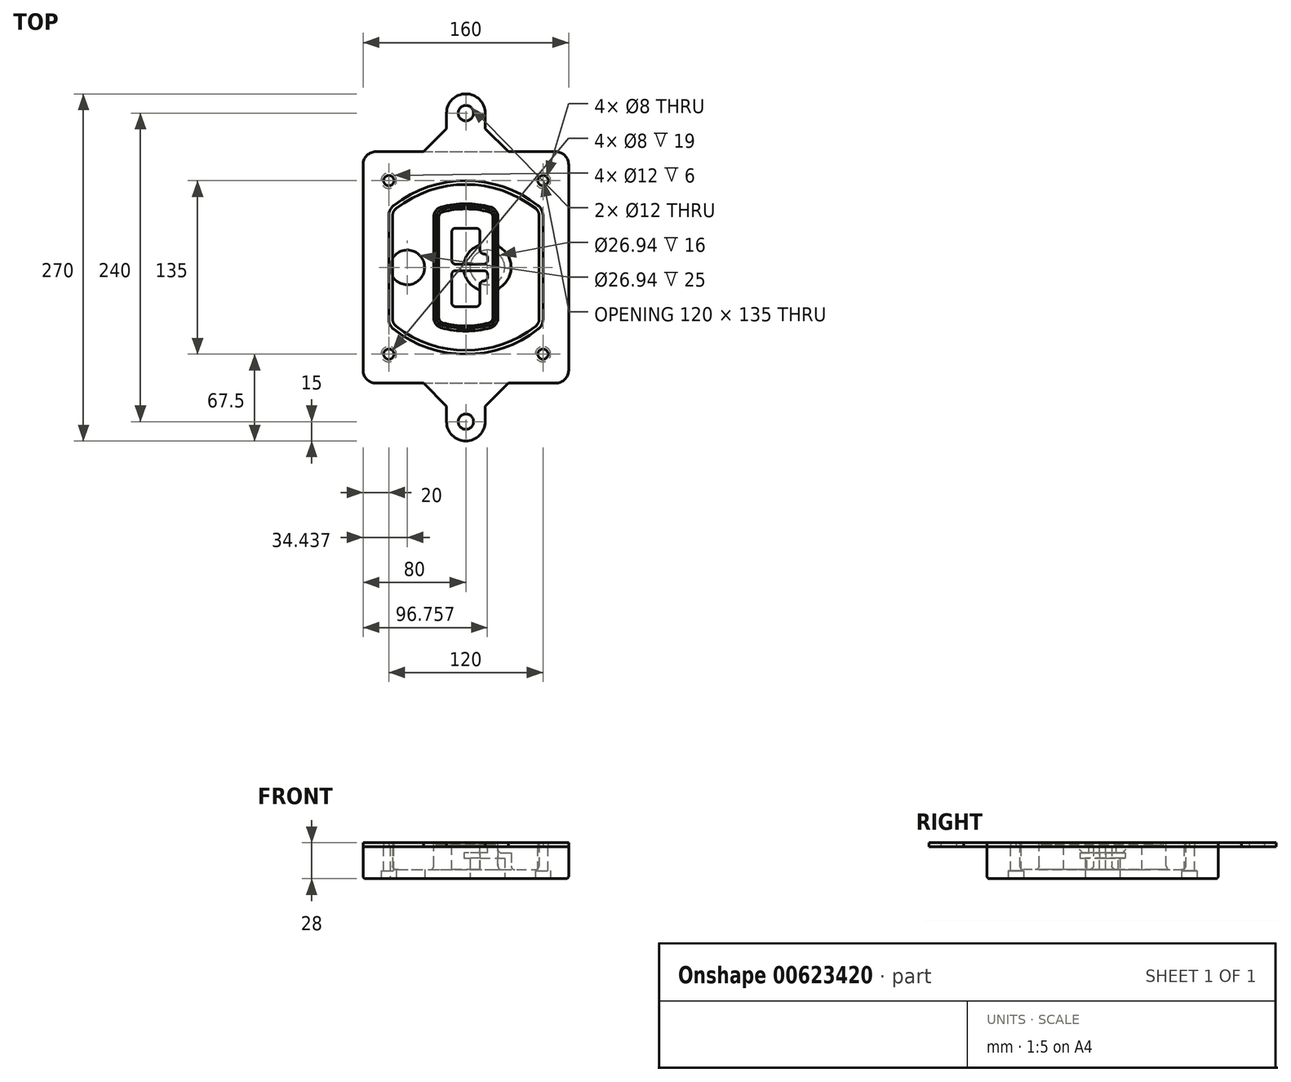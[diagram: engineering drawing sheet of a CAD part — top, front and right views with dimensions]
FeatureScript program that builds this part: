
annotation { "Feature Type Name" : "Feature", "Feature Type Description" : "" }
export const myFeature = defineFeature(function(context is Context, id is Id, definition is map)
    precondition{}
    {
        {
            var Q0;
            Q0=qCreatedBy(makeId("Top.planeOp"),FACE);
            var sketch = newSketch(context, id + "F0", { "sketchPlane" : qUnion([Q0])});
            skPoint(sketch, "E0.rect.middle", {"position": v(0, 0) * mm});
            skLineSegment(sketch, "E1.bottom", {"start": v(-70, -90) * mm, "end": v(70, -90) * mm});
            skLineSegment(sketch, "E1.top", {"start": v(-70, 90) * mm, "end": v(70, 90) * mm});
            skLineSegment(sketch, "E1.left", {"start": v(-80, -80) * mm, "end": v(-80, 80) * mm});
            skLineSegment(sketch, "E1.right", {"start": v(80, -80) * mm, "end": v(80, 80) * mm});
            skLineSegment(sketch, "E2", {"start": v(-80, 90) * mm, "end": v(80, -90) * mm, "construction": true});
            skLineSegment(sketch, "E3", {"start": v(80, 90) * mm, "end": v(-80, -90) * mm, "construction": true});
            skCircle(sketch, "E4", {"center": v(-60, 67.5) * mm, "radius": 4 * mm});
            skCircle(sketch, "E5", {"center": v(60, 67.5) * mm, "radius": 4 * mm});
            skCircle(sketch, "E6", {"center": v(60, -67.5) * mm, "radius": 4 * mm});
            skCircle(sketch, "E7", {"center": v(-60, -67.5) * mm, "radius": 4 * mm});
            skLineSegment(sketch, "E8", {"start": v(-60, 67.5) * mm, "end": v(60, 67.5) * mm, "construction": true});
            skLineSegment(sketch, "E9", {"start": v(60, 67.5) * mm, "end": v(60, -67.5) * mm, "construction": true});
            skLineSegment(sketch, "E10", {"start": v(60, -67.5) * mm, "end": v(-60, -67.5) * mm, "construction": true});
            skLineSegment(sketch, "E11", {"start": v(-60, -67.5) * mm, "end": v(-60, 67.5) * mm, "construction": true});
            skLineSegment(sketch, "E12", {"start": v(-60, 40.3) * mm, "end": v(-60, -40.3) * mm});
            skLineSegment(sketch, "E13", {"start": v(60, 40.3) * mm, "end": v(60, -40.3) * mm});
            skArc(sketch, "E14", {"start": v(56.15, 48.18) * mm, "mid": v(0, 67.5) * mm, "end": v(-56.15, 48.18) * mm});
            skArc(sketch, "E15", {"start": v(-56.15, -48.18) * mm, "mid": v(0, -67.5) * mm, "end": v(56.15, -48.18) * mm});
            skLineSegment(sketch, "E16", {"start": v(-60, 0) * mm, "end": v(60, 0) * mm, "construction": true});
            skPoint(sketch, "E17.visualSharp", {"position": v(-60, -45) * mm});
            skArc(sketch, "E17.filletArc", {"start": v(-60, -40.3) * mm, "mid": v(-58.99, -44.68) * mm, "end": v(-56.15, -48.18) * mm});
            skPoint(sketch, "E18.visualSharp", {"position": v(-60, 45) * mm});
            skArc(sketch, "E18.filletArc", {"start": v(-56.15, 48.18) * mm, "mid": v(-58.99, 44.68) * mm, "end": v(-60, 40.3) * mm});
            skPoint(sketch, "E19.visualSharp", {"position": v(60, 45) * mm});
            skArc(sketch, "E19.filletArc", {"start": v(60, 40.3) * mm, "mid": v(58.99, 44.68) * mm, "end": v(56.15, 48.18) * mm});
            skPoint(sketch, "E20.visualSharp", {"position": v(60, -45) * mm});
            skArc(sketch, "E20.filletArc", {"start": v(56.15, -48.18) * mm, "mid": v(58.99, -44.68) * mm, "end": v(60, -40.3) * mm});
            skPoint(sketch, "E21.visualSharp", {"position": v(-80, 90) * mm});
            skArc(sketch, "E21.filletArc", {"start": v(-70, 90) * mm, "mid": v(-77.07, 87.07) * mm, "end": v(-80, 80) * mm});
            skPoint(sketch, "E22.visualSharp", {"position": v(80, 90) * mm});
            skArc(sketch, "E22.filletArc", {"start": v(80, 80) * mm, "mid": v(77.07, 87.07) * mm, "end": v(70, 90) * mm});
            skPoint(sketch, "E23.visualSharp", {"position": v(80, -90) * mm});
            skArc(sketch, "E23.filletArc", {"start": v(70, -90) * mm, "mid": v(77.07, -87.07) * mm, "end": v(80, -80) * mm});
            skPoint(sketch, "E24.visualSharp", {"position": v(-80, -90) * mm});
            skArc(sketch, "E24.filletArc", {"start": v(-80, -80) * mm, "mid": v(-77.07, -87.07) * mm, "end": v(-70, -90) * mm});
            skArc(sketch, "E25.0", {"start": v(57, 40.3) * mm, "mid": v(56.3, 43.36) * mm, "end": v(54.3, 45.81) * mm});
            skLineSegment(sketch, "E25.1", {"start": v(57, 40.3) * mm, "end": v(57, -40.3) * mm});
            skArc(sketch, "E25.2", {"start": v(54.3, -45.81) * mm, "mid": v(56.3, -43.36) * mm, "end": v(57, -40.3) * mm});
            skArc(sketch, "E25.3", {"start": v(-54.3, -45.81) * mm, "mid": v(0, -64.5) * mm, "end": v(54.3, -45.81) * mm});
            skArc(sketch, "E25.4", {"start": v(-57, -40.3) * mm, "mid": v(-56.3, -43.36) * mm, "end": v(-54.3, -45.81) * mm});
            skArc(sketch, "E25.5", {"start": v(54.3, 45.81) * mm, "mid": v(0, 64.5) * mm, "end": v(-54.3, 45.81) * mm});
            skLineSegment(sketch, "E25.6", {"start": v(-57, 40.3) * mm, "end": v(-57, -40.3) * mm});
            skArc(sketch, "E25.7", {"start": v(-54.3, 45.81) * mm, "mid": v(-56.3, 43.36) * mm, "end": v(-57, 40.3) * mm});
            skArc(sketch, "E26.0", {"start": v(-58.62, 51.33) * mm, "mid": v(-62.58, 46.43) * mm, "end": v(-64, 40.3) * mm});
            skArc(sketch, "E26.1", {"start": v(58.62, 51.33) * mm, "mid": v(0, 71.5) * mm, "end": v(-58.62, 51.33) * mm});
            skArc(sketch, "E26.2", {"start": v(64, 40.3) * mm, "mid": v(62.58, 46.43) * mm, "end": v(58.62, 51.33) * mm});
            skLineSegment(sketch, "E26.3", {"start": v(64, 40.3) * mm, "end": v(64, -40.3) * mm});
            skArc(sketch, "E26.4", {"start": v(58.62, -51.33) * mm, "mid": v(62.58, -46.43) * mm, "end": v(64, -40.3) * mm});
            skLineSegment(sketch, "E26.5", {"start": v(-64, 40.3) * mm, "end": v(-64, -40.3) * mm});
            skArc(sketch, "E26.6", {"start": v(-58.62, -51.33) * mm, "mid": v(0, -71.5) * mm, "end": v(58.62, -51.33) * mm});
            skArc(sketch, "E26.7", {"start": v(-64, -40.3) * mm, "mid": v(-62.58, -46.43) * mm, "end": v(-58.62, -51.33) * mm});
            skSolve(sketch);
        }
        {
            var Q0;
            Q0=makeQuery(id+"F0.imprint","IMPRINT",FACE,{"disambiguationData":[TD([[makeQuery(id+"F0.imprint","IMPRINT",EDGE,{"derivedFrom":sQuery(id+"F0.wireOp",EDGE,"E1.bottom")}),1.0]])]});
            var Q1;
            Q1=makeQuery(id+"F0.imprint","IMPRINT",FACE,{"disambiguationData":[TD([[makeQuery(id+"F0.imprint","IMPRINT",EDGE,{"derivedFrom":sQuery(id+"F0.wireOp",EDGE,"E12")}),1.0]])]});
            var Q2;
            Q2=makeQuery(id+"F0.imprint","IMPRINT",FACE,{"disambiguationData":[TD([[makeQuery(id+"F0.imprint","IMPRINT",EDGE,{"derivedFrom":sQuery(id+"F0.wireOp",EDGE,"E25.0")}),1.0]])]});
            var Q3;
            Q3=makeQuery(id+"F0.imprint","IMPRINT",FACE,{"disambiguationData":[TD([[makeQuery(id+"F0.imprint","IMPRINT",EDGE,{"derivedFrom":sQuery(id+"F0.wireOp",EDGE,"E12")}),-1.0]])]});
            extrude(context, id + "F1", {"entities" : qUnion([Q0, Q1, Q2, Q3]), "oppositeDirection" : true, "depth" : 25 * mm});
        }
        {
            var Q0;
            Q0=makeQuery(id+"F0.imprint","IMPRINT",FACE,{"disambiguationData":[TD([[makeQuery(id+"F0.imprint","IMPRINT",EDGE,{"derivedFrom":sQuery(id+"F0.wireOp",EDGE,"E12")}),1.0]])]});
            extrude(context, id + "F2", {"entities" : qUnion([Q0]), "operationType" : NewBodyOperationType.ADD, "depth" : 3 * mm});
        }
        {
            var Q0;
            Q0=makeQuery(id+"F0.imprint","IMPRINT",FACE,{"disambiguationData":[TD([[makeQuery(id+"F0.imprint","IMPRINT",EDGE,{"derivedFrom":sQuery(id+"F0.wireOp",EDGE,"E25.0")}),1.0]])]});
            extrude(context, id + "F3", {"entities" : qUnion([Q0]), "operationType" : NewBodyOperationType.REMOVE, "oppositeDirection" : true, "depth" : 18 * mm});
        }
        {
            var Q0;
            Q0=makeQuery(id+"F2.opExtrude","CAP_FACE",FACE,{"disambiguationData":[OSD([sQuery(id+"F0.wireOp",EDGE,"E12"),sQuery(id+"F0.wireOp",EDGE,"E13"),sQuery(id+"F0.wireOp",EDGE,"E14"),sQuery(id+"F0.wireOp",EDGE,"E15"),sQuery(id+"F0.wireOp",EDGE,"E17.filletArc"),sQuery(id+"F0.wireOp",EDGE,"E18.filletArc"),sQuery(id+"F0.wireOp",EDGE,"E19.filletArc"),sQuery(id+"F0.wireOp",EDGE,"E20.filletArc"),sQuery(id+"F0.wireOp",EDGE,"E25.0"),sQuery(id+"F0.wireOp",EDGE,"E25.1"),sQuery(id+"F0.wireOp",EDGE,"E25.2"),sQuery(id+"F0.wireOp",EDGE,"E25.3"),sQuery(id+"F0.wireOp",EDGE,"E25.4"),sQuery(id+"F0.wireOp",EDGE,"E25.5"),sQuery(id+"F0.wireOp",EDGE,"E25.6"),sQuery(id+"F0.wireOp",EDGE,"E25.7")])],"isStart":false});
            var sketch = newSketch(context, id + "F4", { "sketchPlane" : qUnion([Q0])});
            skArc(sketch, "E27.0", {"start": v(-19.08, -46.97) * mm, "mid": v(0, -49.5) * mm, "end": v(19.08, -46.97) * mm});
            skArc(sketch, "E28.0", {"start": v(19.08, 46.97) * mm, "mid": v(0, 49.5) * mm, "end": v(-19.08, 46.97) * mm});
            skLineSegment(sketch, "E29", {"start": v(-25, 39.25) * mm, "end": v(-25, -39.25) * mm});
            skLineSegment(sketch, "E30", {"start": v(25, 39.25) * mm, "end": v(25, -39.25) * mm});
            skLineSegment(sketch, "E31", {"start": v(-25, 45.1) * mm, "end": v(25, 45.1) * mm, "construction": true});
            skLineSegment(sketch, "E32", {"start": v(-25, -45.1) * mm, "end": v(25, -45.1) * mm, "construction": true});
            skPoint(sketch, "E33.visualSharp", {"position": v(-25, 45.1) * mm});
            skArc(sketch, "E33.filletArc", {"start": v(-19.08, 46.97) * mm, "mid": v(-23.35, 44.11) * mm, "end": v(-25, 39.25) * mm});
            skPoint(sketch, "E34.visualSharp", {"position": v(25, 45.1) * mm});
            skArc(sketch, "E34.filletArc", {"start": v(25, 39.25) * mm, "mid": v(23.35, 44.11) * mm, "end": v(19.08, 46.97) * mm});
            skPoint(sketch, "E35.visualSharp", {"position": v(25, -45.1) * mm});
            skArc(sketch, "E35.filletArc", {"start": v(19.08, -46.97) * mm, "mid": v(23.35, -44.11) * mm, "end": v(25, -39.25) * mm});
            skPoint(sketch, "E36.visualSharp", {"position": v(-25, -45.1) * mm});
            skArc(sketch, "E36.filletArc", {"start": v(-25, -39.25) * mm, "mid": v(-23.35, -44.11) * mm, "end": v(-19.08, -46.97) * mm});
            skArc(sketch, "E37.0", {"start": v(54.3, 45.81) * mm, "mid": v(0, 64.5) * mm, "end": v(-54.3, 45.81) * mm});
            skArc(sketch, "E37.1", {"start": v(-54.3, 45.81) * mm, "mid": v(-56.3, 43.36) * mm, "end": v(-57, 40.3) * mm});
            skLineSegment(sketch, "E37.2", {"start": v(-57, 40.3) * mm, "end": v(-57, -40.3) * mm});
            skArc(sketch, "E37.3", {"start": v(-57, -40.3) * mm, "mid": v(-56.3, -43.36) * mm, "end": v(-54.3, -45.81) * mm});
            skArc(sketch, "E37.4", {"start": v(-54.3, -45.81) * mm, "mid": v(0, -64.5) * mm, "end": v(54.3, -45.81) * mm});
            skArc(sketch, "E37.5", {"start": v(54.3, -45.81) * mm, "mid": v(56.3, -43.36) * mm, "end": v(57, -40.3) * mm});
            skLineSegment(sketch, "E37.6", {"start": v(57, 40.3) * mm, "end": v(57, -40.3) * mm});
            skArc(sketch, "E37.7", {"start": v(57, 40.3) * mm, "mid": v(56.3, 43.36) * mm, "end": v(54.3, 45.81) * mm});
            skLineSegment(sketch, "E38.0", {"start": v(23, 39.25) * mm, "end": v(23, -39.25) * mm});
            skArc(sketch, "E38.1", {"start": v(18.56, -45.04) * mm, "mid": v(21.76, -42.9) * mm, "end": v(23, -39.25) * mm});
            skArc(sketch, "E38.2", {"start": v(-18.56, -45.04) * mm, "mid": v(0, -47.5) * mm, "end": v(18.56, -45.04) * mm});
            skArc(sketch, "E38.3", {"start": v(-23, -39.25) * mm, "mid": v(-21.76, -42.9) * mm, "end": v(-18.56, -45.04) * mm});
            skLineSegment(sketch, "E38.4", {"start": v(-23, 39.25) * mm, "end": v(-23, -39.25) * mm});
            skArc(sketch, "E38.5", {"start": v(23, 39.25) * mm, "mid": v(21.76, 42.9) * mm, "end": v(18.56, 45.04) * mm});
            skArc(sketch, "E38.6", {"start": v(-18.56, 45.04) * mm, "mid": v(-21.76, 42.9) * mm, "end": v(-23, 39.25) * mm});
            skArc(sketch, "E38.7", {"start": v(18.56, 45.04) * mm, "mid": v(0, 47.5) * mm, "end": v(-18.56, 45.04) * mm});
            skArc(sketch, "E39.0", {"start": v(21, 39.25) * mm, "mid": v(20.18, 41.68) * mm, "end": v(18.04, 43.1) * mm});
            skLineSegment(sketch, "E39.1", {"start": v(21, 39.25) * mm, "end": v(21, -39.25) * mm});
            skArc(sketch, "E39.2", {"start": v(18.04, -43.1) * mm, "mid": v(20.18, -41.68) * mm, "end": v(21, -39.25) * mm});
            skArc(sketch, "E39.3", {"start": v(-18.04, -43.1) * mm, "mid": v(0, -45.5) * mm, "end": v(18.04, -43.1) * mm});
            skArc(sketch, "E39.4", {"start": v(-21, -39.25) * mm, "mid": v(-20.18, -41.68) * mm, "end": v(-18.04, -43.1) * mm});
            skArc(sketch, "E39.5", {"start": v(18.04, 43.1) * mm, "mid": v(0, 45.5) * mm, "end": v(-18.04, 43.1) * mm});
            skLineSegment(sketch, "E39.6", {"start": v(-21, 39.25) * mm, "end": v(-21, -39.25) * mm});
            skArc(sketch, "E39.7", {"start": v(-18.04, 43.1) * mm, "mid": v(-20.18, 41.68) * mm, "end": v(-21, 39.25) * mm});
            skLineSegment(sketch, "E40", {"start": v(-25, 0) * mm, "end": v(25, 0) * mm, "construction": true});
            skLineSegment(sketch, "E41", {"start": v(-11, 5.5) * mm, "end": v(-11, 27.5) * mm});
            skLineSegment(sketch, "E42", {"start": v(-8, 30.5) * mm, "end": v(8, 30.5) * mm});
            skLineSegment(sketch, "E43", {"start": v(11, 27.5) * mm, "end": v(11, 13.5) * mm});
            skLineSegment(sketch, "E44", {"start": v(14, 10.5) * mm, "end": v(14, 10.5) * mm});
            skLineSegment(sketch, "E45", {"start": v(17, 7.5) * mm, "end": v(17, 5.5) * mm});
            skLineSegment(sketch, "E46", {"start": v(14, 2.5) * mm, "end": v(-8, 2.5) * mm});
            skPoint(sketch, "E47.visualSharp", {"position": v(-11, 30.5) * mm});
            skArc(sketch, "E47.filletArc", {"start": v(-8, 30.5) * mm, "mid": v(-10.12, 29.62) * mm, "end": v(-11, 27.5) * mm});
            skPoint(sketch, "E48.visualSharp", {"position": v(11, 30.5) * mm});
            skArc(sketch, "E48.filletArc", {"start": v(11, 27.5) * mm, "mid": v(10.12, 29.62) * mm, "end": v(8, 30.5) * mm});
            skPoint(sketch, "E49.visualSharp", {"position": v(11, 10.5) * mm});
            skArc(sketch, "E49.filletArc", {"start": v(11, 13.5) * mm, "mid": v(11.88, 11.38) * mm, "end": v(14, 10.5) * mm});
            skPoint(sketch, "E50.visualSharp", {"position": v(17, 10.5) * mm});
            skArc(sketch, "E50.filletArc", {"start": v(17, 7.5) * mm, "mid": v(16.12, 9.62) * mm, "end": v(14, 10.5) * mm});
            skPoint(sketch, "E51.visualSharp", {"position": v(17, 2.5) * mm});
            skArc(sketch, "E51.filletArc", {"start": v(14, 2.5) * mm, "mid": v(16.12, 3.38) * mm, "end": v(17, 5.5) * mm});
            skPoint(sketch, "E52.visualSharp", {"position": v(-11, 2.5) * mm});
            skArc(sketch, "E52.filletArc", {"start": v(-11, 5.5) * mm, "mid": v(-10.12, 3.38) * mm, "end": v(-8, 2.5) * mm});
            skLineSegment(sketch, "E53.0.MirrorCS", {"start": v(14, -2.5) * mm, "end": v(-8, -2.5) * mm});
            skArc(sketch, "E54.0.MirrorCS", {"start": v(-11, -5.5) * mm, "mid": v(-10.12, -3.38) * mm, "end": v(-8, -2.5) * mm});
            skLineSegment(sketch, "E55.0.MirrorCS", {"start": v(-11, -5.5) * mm, "end": v(-11, -27.5) * mm});
            skArc(sketch, "E56.0.MirrorCS", {"start": v(-8, -30.5) * mm, "mid": v(-10.12, -29.62) * mm, "end": v(-11, -27.5) * mm});
            skLineSegment(sketch, "E57.0.MirrorCS", {"start": v(-8, -30.5) * mm, "end": v(8, -30.5) * mm});
            skArc(sketch, "E58.0.MirrorCS", {"start": v(11, -27.5) * mm, "mid": v(10.12, -29.62) * mm, "end": v(8, -30.5) * mm});
            skLineSegment(sketch, "E59.0.MirrorCS", {"start": v(11, -27.5) * mm, "end": v(11, -13.5) * mm});
            skArc(sketch, "E60.0.MirrorCS", {"start": v(11, -13.5) * mm, "mid": v(11.88, -11.38) * mm, "end": v(14, -10.5) * mm});
            skArc(sketch, "E61.0.MirrorCS", {"start": v(17, -7.5) * mm, "mid": v(16.12, -9.62) * mm, "end": v(14, -10.5) * mm});
            skLineSegment(sketch, "E62.0.MirrorCS", {"start": v(17, -7.5) * mm, "end": v(17, -5.5) * mm});
            skArc(sketch, "E63.0.MirrorCS", {"start": v(14, -2.5) * mm, "mid": v(16.12, -3.38) * mm, "end": v(17, -5.5) * mm});
            skSolve(sketch);
        }
        {
            var Q0;
            Q0=makeQuery(id+"F4.imprint","IMPRINT",FACE,{"disambiguationData":[TD([[makeQuery(id+"F4.imprint","IMPRINT",EDGE,{"derivedFrom":sQuery(id+"F4.wireOp",EDGE,"E27.0")}),1.0]])]});
            var Q1;
            Q1=makeQuery(id+"F4.imprint","IMPRINT",FACE,{"disambiguationData":[TD([[makeQuery(id+"F4.imprint","IMPRINT",EDGE,{"derivedFrom":sQuery(id+"F4.wireOp",EDGE,"E38.0")}),-1.0]])]});
            var Q2;
            Q2=makeQuery(id+"F4.imprint","IMPRINT",FACE,{"disambiguationData":[TD([[makeQuery(id+"F4.imprint","IMPRINT",EDGE,{"derivedFrom":sQuery(id+"F4.wireOp",EDGE,"E39.0")}),1.0]])]});
            extrude(context, id + "F5", {"entities" : qUnion([Q0, Q1, Q2]), "operationType" : NewBodyOperationType.ADD, "endBound" : BoundingType.UP_TO_NEXT, "oppositeDirection" : true, "depth" : 25 * mm});
        }
        {
            var Q0;
            Q0=makeQuery(id+"F4.imprint","IMPRINT",FACE,{"disambiguationData":[TD([[makeQuery(id+"F4.imprint","IMPRINT",EDGE,{"derivedFrom":sQuery(id+"F4.wireOp",EDGE,"E38.0")}),-1.0]])]});
            extrude(context, id + "F6", {"entities" : qUnion([Q0]), "operationType" : NewBodyOperationType.REMOVE, "oppositeDirection" : true, "depth" : 2 * mm});
        }
        {
            var Q0;
            Q0=makeQuery(id+"F1.opExtrude","CAP_FACE",FACE,{"disambiguationData":[OSD([sQuery(id+"F0.wireOp",EDGE,"E1.bottom"),sQuery(id+"F0.wireOp",EDGE,"E1.top"),sQuery(id+"F0.wireOp",EDGE,"E1.left"),sQuery(id+"F0.wireOp",EDGE,"E1.right"),sQuery(id+"F0.wireOp",EDGE,"E4"),sQuery(id+"F0.wireOp",EDGE,"E5"),sQuery(id+"F0.wireOp",EDGE,"E6"),sQuery(id+"F0.wireOp",EDGE,"E7"),sQuery(id+"F0.wireOp",EDGE,"E21.filletArc"),sQuery(id+"F0.wireOp",EDGE,"E22.filletArc"),sQuery(id+"F0.wireOp",EDGE,"E23.filletArc"),sQuery(id+"F0.wireOp",EDGE,"E24.filletArc")])],"isStart":false});
            var sketch = newSketch(context, id + "F7", { "sketchPlane" : qUnion([Q0])});
            skCircle(sketch, "E64", {"center": v(16.76, 0) * mm, "radius": 13.47 * mm});
            skCircle(sketch, "E65", {"center": v(-45.56, 0) * mm, "radius": 13.47 * mm});
            skLineSegment(sketch, "E66", {"start": v(80, 0) * mm, "end": v(-80, 0) * mm});
            skCircle(sketch, "E67", {"center": v(16.76, 0) * mm, "radius": 18.47 * mm});
            skCircle(sketch, "E68", {"center": v(60, -67.5) * mm, "radius": 6 * mm});
            skCircle(sketch, "E69", {"center": v(-60, -67.5) * mm, "radius": 6 * mm});
            skCircle(sketch, "E70", {"center": v(-60, 67.5) * mm, "radius": 6 * mm});
            skCircle(sketch, "E71", {"center": v(60, 67.5) * mm, "radius": 6 * mm});
            skSolve(sketch);
        }
        {
            var Q0;
            {var subQ1=sQuery(id+"F7.wireOp",EDGE,"E66");var subQ4=sQuery(id+"F7.wireOp",EDGE,"E64");var subQ6=makeQuery(id+"F7.imprint","INTERSECT",VERTEX,{"disambiguationData":[OD(0.0)],"derivedFrom":[subQ4,subQ1]});Q0=makeQuery(id+"F7.imprint","IMPRINT",FACE,{"disambiguationData":[TD([[makeQuery(id+"F7.imprint","IMPRINT",EDGE,{"disambiguationData":[TD([[subQ6,-1.0]])],"derivedFrom":subQ4}),-1.0]])]});}
            var Q1;
            {var subQ0=sQuery(id+"F7.wireOp",EDGE,"E66");var subQ1=sQuery(id+"F7.wireOp",EDGE,"E64");var subQ3=makeQuery(id+"F7.imprint","INTERSECT",VERTEX,{"disambiguationData":[OD(0.0)],"derivedFrom":[subQ1,subQ0]});Q1=makeQuery(id+"F7.imprint","IMPRINT",FACE,{"disambiguationData":[TD([[makeQuery(id+"F7.imprint","IMPRINT",EDGE,{"disambiguationData":[TD([[subQ3,-1.0]])],"derivedFrom":subQ1}),1.0]])]});}
            var Q2;
            {var subQ0=sQuery(id+"F7.wireOp",EDGE,"E66");var subQ1=sQuery(id+"F7.wireOp",EDGE,"E64");var subQ3=makeQuery(id+"F7.imprint","INTERSECT",VERTEX,{"disambiguationData":[OD(0.0)],"derivedFrom":[subQ1,subQ0]});Q2=makeQuery(id+"F7.imprint","IMPRINT",FACE,{"disambiguationData":[TD([[makeQuery(id+"F7.imprint","IMPRINT",EDGE,{"disambiguationData":[TD([[subQ3,1.0]])],"derivedFrom":subQ1}),1.0]])]});}
            var Q3;
            {var subQ1=sQuery(id+"F7.wireOp",EDGE,"E66");var subQ4=sQuery(id+"F7.wireOp",EDGE,"E64");var subQ6=makeQuery(id+"F7.imprint","INTERSECT",VERTEX,{"disambiguationData":[OD(0.0)],"derivedFrom":[subQ4,subQ1]});Q3=makeQuery(id+"F7.imprint","IMPRINT",FACE,{"disambiguationData":[TD([[makeQuery(id+"F7.imprint","IMPRINT",EDGE,{"disambiguationData":[TD([[subQ6,1.0]])],"derivedFrom":subQ4}),-1.0]])]});}
            extrude(context, id + "F8", {"entities" : qUnion([Q0, Q1, Q2, Q3]), "operationType" : NewBodyOperationType.ADD, "oppositeDirection" : true, "depth" : 20 * mm});
        }
        {
            var Q0;
            {var subQ0=sQuery(id+"F7.wireOp",EDGE,"E66");var subQ1=sQuery(id+"F7.wireOp",EDGE,"E64");var subQ3=makeQuery(id+"F7.imprint","INTERSECT",VERTEX,{"disambiguationData":[OD(0.0)],"derivedFrom":[subQ1,subQ0]});Q0=makeQuery(id+"F7.imprint","IMPRINT",FACE,{"disambiguationData":[TD([[makeQuery(id+"F7.imprint","IMPRINT",EDGE,{"disambiguationData":[TD([[subQ3,-1.0]])],"derivedFrom":subQ1}),1.0]])]});}
            var Q1;
            {var subQ0=sQuery(id+"F7.wireOp",EDGE,"E66");var subQ1=sQuery(id+"F7.wireOp",EDGE,"E64");var subQ3=makeQuery(id+"F7.imprint","INTERSECT",VERTEX,{"disambiguationData":[OD(0.0)],"derivedFrom":[subQ1,subQ0]});Q1=makeQuery(id+"F7.imprint","IMPRINT",FACE,{"disambiguationData":[TD([[makeQuery(id+"F7.imprint","IMPRINT",EDGE,{"disambiguationData":[TD([[subQ3,1.0]])],"derivedFrom":subQ1}),1.0]])]});}
            extrude(context, id + "F9", {"entities" : qUnion([Q0, Q1]), "operationType" : NewBodyOperationType.REMOVE, "oppositeDirection" : true, "depth" : 16 * mm});
        }
        {
            var Q0;
            {var subQ0=sQuery(id+"F7.wireOp",EDGE,"E66");var subQ1=sQuery(id+"F7.wireOp",EDGE,"E65");var subQ3=makeQuery(id+"F7.imprint","INTERSECT",VERTEX,{"disambiguationData":[OD(0.0)],"derivedFrom":[subQ1,subQ0]});Q0=makeQuery(id+"F7.imprint","IMPRINT",FACE,{"disambiguationData":[TD([[makeQuery(id+"F7.imprint","IMPRINT",EDGE,{"disambiguationData":[TD([[subQ3,-1.0]])],"derivedFrom":subQ1}),1.0]])]});}
            var Q1;
            {var subQ0=sQuery(id+"F7.wireOp",EDGE,"E66");var subQ1=sQuery(id+"F7.wireOp",EDGE,"E65");var subQ3=makeQuery(id+"F7.imprint","INTERSECT",VERTEX,{"disambiguationData":[OD(0.0)],"derivedFrom":[subQ1,subQ0]});Q1=makeQuery(id+"F7.imprint","IMPRINT",FACE,{"disambiguationData":[TD([[makeQuery(id+"F7.imprint","IMPRINT",EDGE,{"disambiguationData":[TD([[subQ3,1.0]])],"derivedFrom":subQ1}),1.0]])]});}
            extrude(context, id + "F10", {"entities" : qUnion([Q0, Q1]), "operationType" : NewBodyOperationType.REMOVE, "oppositeDirection" : true, "depth" : 25 * mm});
        }
        {
            var Q0;
            Q0=makeQuery(id+"F7.imprint","IMPRINT",FACE,{"disambiguationData":[TD([[makeQuery(id+"F7.imprint","IMPRINT",EDGE,{"derivedFrom":sQuery(id+"F7.wireOp",EDGE,"E68")}),1.0]])]});
            var Q1;
            Q1=makeQuery(id+"F7.imprint","IMPRINT",FACE,{"disambiguationData":[TD([[makeQuery(id+"F7.imprint","IMPRINT",EDGE,{"derivedFrom":makeQuery(id+"F1.opExtrude","CAP_EDGE",EDGE,{"disambiguationData":[OSD([sQuery(id+"F0.wireOp",EDGE,"E5")])],"isStart":false})}),-1.0]])]});
            var Q2;
            Q2=makeQuery(id+"F7.imprint","IMPRINT",FACE,{"disambiguationData":[TD([[makeQuery(id+"F7.imprint","IMPRINT",EDGE,{"derivedFrom":sQuery(id+"F7.wireOp",EDGE,"E69")}),1.0]])]});
            var Q3;
            Q3=makeQuery(id+"F7.imprint","IMPRINT",FACE,{"disambiguationData":[TD([[makeQuery(id+"F7.imprint","IMPRINT",EDGE,{"derivedFrom":makeQuery(id+"F1.opExtrude","CAP_EDGE",EDGE,{"disambiguationData":[OSD([sQuery(id+"F0.wireOp",EDGE,"E4")])],"isStart":false})}),-1.0]])]});
            var Q4;
            Q4=makeQuery(id+"F7.imprint","IMPRINT",FACE,{"disambiguationData":[TD([[makeQuery(id+"F7.imprint","IMPRINT",EDGE,{"derivedFrom":sQuery(id+"F7.wireOp",EDGE,"E70")}),1.0]])]});
            var Q5;
            Q5=makeQuery(id+"F7.imprint","IMPRINT",FACE,{"disambiguationData":[TD([[makeQuery(id+"F7.imprint","IMPRINT",EDGE,{"derivedFrom":makeQuery(id+"F1.opExtrude","CAP_EDGE",EDGE,{"disambiguationData":[OSD([sQuery(id+"F0.wireOp",EDGE,"E7")])],"isStart":false})}),-1.0]])]});
            var Q6;
            Q6=makeQuery(id+"F7.imprint","IMPRINT",FACE,{"disambiguationData":[TD([[makeQuery(id+"F7.imprint","IMPRINT",EDGE,{"derivedFrom":sQuery(id+"F7.wireOp",EDGE,"E71")}),1.0]])]});
            var Q7;
            Q7=makeQuery(id+"F7.imprint","IMPRINT",FACE,{"disambiguationData":[TD([[makeQuery(id+"F7.imprint","IMPRINT",EDGE,{"derivedFrom":makeQuery(id+"F1.opExtrude","CAP_EDGE",EDGE,{"disambiguationData":[OSD([sQuery(id+"F0.wireOp",EDGE,"E6")])],"isStart":false})}),-1.0]])]});
            extrude(context, id + "F11", {"entities" : qUnion([Q0, Q1, Q2, Q3, Q4, Q5, Q6, Q7]), "operationType" : NewBodyOperationType.REMOVE, "oppositeDirection" : true, "depth" : 6 * mm});
        }
        {
            var Q0;
            Q0=makeQuery(id+"F9.boolean.opBoolean","COPY",FACE,{"derivedFrom":makeQuery(id+"F9.opExtrude","CAP_FACE",FACE,{"disambiguationData":[OSD([sQuery(id+"F7.wireOp",EDGE,"E64")])],"isStart":false})});
            var sketch = newSketch(context, id + "F12", { "sketchPlane" : qUnion([Q0])});
            skArc(sketch, "E72.0", {"start": v(11, 17.55) * mm, "mid": v(2.57, 11.82) * mm, "end": v(-1.54, 2.5) * mm});
            skArc(sketch, "E72.1", {"start": v(-1.54, -2.5) * mm, "mid": v(2.57, -11.82) * mm, "end": v(11, -17.55) * mm});
            skLineSegment(sketch, "E73", {"start": v(-1.54, -2.5) * mm, "end": v(14, -2.5) * mm});
            skLineSegment(sketch, "E74.0", {"start": v(14, 2.5) * mm, "end": v(-1.54, 2.5) * mm});
            skArc(sketch, "E74.1", {"start": v(14, 2.5) * mm, "mid": v(16.12, 3.38) * mm, "end": v(17, 5.5) * mm});
            skLineSegment(sketch, "E74.2", {"start": v(17, 7.5) * mm, "end": v(17, 5.5) * mm});
            skArc(sketch, "E74.3", {"start": v(17, 7.5) * mm, "mid": v(16.12, 9.62) * mm, "end": v(14, 10.5) * mm});
            skArc(sketch, "E74.4", {"start": v(11, 13.5) * mm, "mid": v(11.88, 11.38) * mm, "end": v(14, 10.5) * mm});
            skLineSegment(sketch, "E74.5", {"start": v(11, 17.55) * mm, "end": v(11, 13.5) * mm});
            skLineSegment(sketch, "E74.7", {"start": v(14, -2.5) * mm, "end": v(-1.54, -2.5) * mm});
            skArc(sketch, "E74.8", {"start": v(14, -2.5) * mm, "mid": v(16.12, -3.38) * mm, "end": v(17, -5.5) * mm});
            skLineSegment(sketch, "E74.9", {"start": v(17, -7.5) * mm, "end": v(17, -5.5) * mm});
            skArc(sketch, "E74.10", {"start": v(17, -7.5) * mm, "mid": v(16.12, -9.62) * mm, "end": v(14, -10.5) * mm});
            skArc(sketch, "E74.11", {"start": v(11, -13.5) * mm, "mid": v(11.88, -11.38) * mm, "end": v(14, -10.5) * mm});
            skLineSegment(sketch, "E74.12", {"start": v(11, -17.55) * mm, "end": v(11, -13.5) * mm});
            skPoint(sketch, "E75.orphan", {"position": v(11, -27.5) * mm});
            skPoint(sketch, "E76.orphan", {"position": v(-8, -2.5) * mm});
            skPoint(sketch, "E77.orphan", {"position": v(-8, 2.5) * mm});
            skPoint(sketch, "E78.orphan", {"position": v(11, 27.5) * mm});
            skSolve(sketch);
        }
        {
            var Q0;
            {var subQ7=sQuery(id+"F12.wireOp",EDGE,"E72.0");var subQ14=sQuery(id+"F12.wireOp",EDGE,"E72.1");var subQ16=sQuery(id+"F12.wireOp",EDGE,"E74.1");var subQ18=sQuery(id+"F12.wireOp",EDGE,"E74.8");Q0=qUnion([makeQuery(id+"F12.imprint","IMPRINT",FACE,{"disambiguationData":[TD([[makeQuery(id+"F12.imprint","IMPRINT",EDGE,{"derivedFrom":subQ7}),1.0]])]}),makeQuery(id+"F12.imprint","IMPRINT",FACE,{"disambiguationData":[TD([[makeQuery(id+"F12.imprint","IMPRINT",EDGE,{"derivedFrom":subQ14}),1.0]])]}),makeQuery(id+"F12.imprint","IMPRINT",FACE,{"disambiguationData":[TD([[makeQuery(id+"F12.imprint","IMPRINT",EDGE,{"derivedFrom":subQ16}),1.0]])]}),makeQuery(id+"F12.imprint","IMPRINT",FACE,{"disambiguationData":[TD([[makeQuery(id+"F12.imprint","IMPRINT",EDGE,{"derivedFrom":subQ18}),-1.0]])]})]);}
            var Q1;
            Q1=makeQuery(id+"F5.boolean.opBoolean","SPLIT",FACE,{"disambiguationData":[TD([makeQuery(id+"F5.opExtrude","SWEPT_FACE",FACE,{"disambiguationData":[OSD([sQuery(id+"F4.wireOp",EDGE,"E41")])]})])],"derivedFrom":makeQuery(id+"F3.boolean.opBoolean","COPY",FACE,{"derivedFrom":makeQuery(id+"F3.opExtrude","CAP_FACE",FACE,{"disambiguationData":[OSD([sQuery(id+"F0.wireOp",EDGE,"E25.0"),sQuery(id+"F0.wireOp",EDGE,"E25.1"),sQuery(id+"F0.wireOp",EDGE,"E25.2"),sQuery(id+"F0.wireOp",EDGE,"E25.3"),sQuery(id+"F0.wireOp",EDGE,"E25.4"),sQuery(id+"F0.wireOp",EDGE,"E25.5"),sQuery(id+"F0.wireOp",EDGE,"E25.6"),sQuery(id+"F0.wireOp",EDGE,"E25.7")])],"isStart":false})})});
            extrude(context, id + "F13", {"entities" : qUnion([Q0]), "operationType" : NewBodyOperationType.REMOVE, "endBound" : BoundingType.UP_TO_SURFACE, "endBoundEntityFace" : qUnion([Q1]), "depth" : 25 * mm});
        }
        {
            var Q0;
            Q0=makeQuery(id+"F3.boolean.opBoolean","COPY",EDGE,{"derivedFrom":makeQuery(id+"F3.opExtrude","CAP_EDGE",EDGE,{"disambiguationData":[OSD([sQuery(id+"F0.wireOp",EDGE,"E25.6")])],"isStart":false})});
            var Q1;
            Q1=makeQuery(id+"F8.boolean.opBoolean","INTERSECT",EDGE,{"derivedFrom":[makeQuery(id+"F5.opExtrude","SWEPT_FACE",FACE,{"disambiguationData":[OSD([sQuery(id+"F4.wireOp",EDGE,"E30")])]}),makeQuery(id+"F8.opExtrude","CAP_FACE",FACE,{"disambiguationData":[OSD([sQuery(id+"F7.wireOp",EDGE,"E67")])],"isStart":false})]});
            var Q2;
            Q2=makeQuery(id+"F8.boolean.opBoolean","INTERSECT",EDGE,{"disambiguationData":[OD(1.0)],"derivedFrom":[makeQuery(id+"F5.opExtrude","SWEPT_FACE",FACE,{"disambiguationData":[OSD([sQuery(id+"F4.wireOp",EDGE,"E30")])]}),makeQuery(id+"F8.opExtrude","SWEPT_FACE",FACE,{"disambiguationData":[OSD([sQuery(id+"F7.wireOp",EDGE,"E67")])]})]});
            var Q3;
            {var subQ0=sQuery(id+"F4.wireOp",EDGE,"E30");Q3=makeQuery(id+"F8.boolean.opBoolean","SPLIT",EDGE,{"disambiguationData":[TD([makeQuery(id+"F5.opExtrude","SWEPT_FACE",FACE,{"disambiguationData":[OSD([sQuery(id+"F4.wireOp",EDGE,"E35.filletArc")])]})])],"derivedFrom":makeQuery(id+"F5.opExtrude","CAP_EDGE",EDGE,{"disambiguationData":[OSD([subQ0])],"isStart":false})});}
            var Q4;
            {var subQ0=sQuery(id+"F0.wireOp",EDGE,"E25.7");var subQ1=sQuery(id+"F0.wireOp",EDGE,"E25.1");var subQ2=sQuery(id+"F0.wireOp",EDGE,"E25.6");var subQ3=sQuery(id+"F0.wireOp",EDGE,"E25.5");var subQ4=sQuery(id+"F0.wireOp",EDGE,"E25.4");var subQ5=sQuery(id+"F0.wireOp",EDGE,"E25.0");var subQ6=sQuery(id+"F0.wireOp",EDGE,"E25.2");var subQ7=sQuery(id+"F0.wireOp",EDGE,"E25.3");Q4=makeQuery(id+"F8.boolean.opBoolean","INTERSECT",EDGE,{"derivedFrom":[makeQuery(id+"F5.boolean.opBoolean","SPLIT",FACE,{"disambiguationData":[TD([makeQuery(id+"F2.opExtrude","SWEPT_FACE",FACE,{"disambiguationData":[OSD([subQ5])]})])],"derivedFrom":makeQuery(id+"F3.boolean.opBoolean","COPY",FACE,{"derivedFrom":makeQuery(id+"F3.opExtrude","CAP_FACE",FACE,{"disambiguationData":[OSD([subQ5,subQ1,subQ6,subQ7,subQ4,subQ3,subQ2,subQ0])],"isStart":false})})}),makeQuery(id+"F8.opExtrude","SWEPT_FACE",FACE,{"disambiguationData":[OSD([sQuery(id+"F7.wireOp",EDGE,"E67")])]})]});}
            var Q5;
            Q5=makeQuery(id+"F8.boolean.opBoolean","INTERSECT",EDGE,{"disambiguationData":[OD(0.0)],"derivedFrom":[makeQuery(id+"F5.opExtrude","SWEPT_FACE",FACE,{"disambiguationData":[OSD([sQuery(id+"F4.wireOp",EDGE,"E30")])]}),makeQuery(id+"F8.opExtrude","SWEPT_FACE",FACE,{"disambiguationData":[OSD([sQuery(id+"F7.wireOp",EDGE,"E67")])]})]});
            fillet(context, id + "F14", {"entities" : qUnion([Q0, Q1, Q2, Q3, Q4, Q5]), "radius" : 3 * mm, "tangentPropagation" : true, "allowEdgeOverflow" : false});
        }
        {
            var Q0;
            Q0=makeQuery(id+"F1.opExtrude","CAP_EDGE",EDGE,{"disambiguationData":[OSD([sQuery(id+"F0.wireOp",EDGE,"E1.bottom")])],"isStart":false});
            fillet(context, id + "F15", {"entities" : qUnion([Q0]), "radius" : 2 * mm, "tangentPropagation" : true, "allowEdgeOverflow" : false});
        }
        {
            var Q0;
            {var subQ0=sQuery(id+"F0.wireOp",EDGE,"E21.filletArc");var subQ1=sQuery(id+"F0.wireOp",EDGE,"E7");var subQ2=sQuery(id+"F0.wireOp",EDGE,"E6");var subQ3=sQuery(id+"F0.wireOp",EDGE,"E5");var subQ4=sQuery(id+"F0.wireOp",EDGE,"E4");var subQ5=sQuery(id+"F0.wireOp",EDGE,"E22.filletArc");var subQ6=sQuery(id+"F0.wireOp",EDGE,"E1.bottom");var subQ7=sQuery(id+"F0.wireOp",EDGE,"E1.right");var subQ8=sQuery(id+"F0.wireOp",EDGE,"E1.top");var subQ9=sQuery(id+"F0.wireOp",EDGE,"E1.left");var subQ10=sQuery(id+"F0.wireOp",EDGE,"E23.filletArc");var subQ11=sQuery(id+"F0.wireOp",EDGE,"E24.filletArc");Q0=makeQuery(id+"F2.boolean.opBoolean","SPLIT",FACE,{"disambiguationData":[TD([makeQuery(id+"F1.opExtrude","SWEPT_FACE",FACE,{"disambiguationData":[OSD([subQ6])]})])],"derivedFrom":makeQuery(id+"F1.opExtrude","CAP_FACE",FACE,{"disambiguationData":[OSD([subQ6,subQ8,subQ9,subQ7,subQ4,subQ3,subQ2,subQ1,subQ0,subQ5,subQ10,subQ11])],"isStart":true})});}
            var sketch = newSketch(context, id + "F16", { "sketchPlane" : qUnion([Q0])});
            skCircle(sketch, "E79.0", {"center": v(60, 67.5) * mm, "radius": 4 * mm});
            skCircle(sketch, "E79.1", {"center": v(-60, 67.5) * mm, "radius": 4 * mm});
            skCircle(sketch, "E79.2", {"center": v(-60, -67.5) * mm, "radius": 4 * mm});
            skCircle(sketch, "E79.3", {"center": v(60, -67.5) * mm, "radius": 4 * mm});
            skLineSegment(sketch, "E79.4", {"start": v(-80, -80) * mm, "end": v(-80, 80) * mm});
            skLineSegment(sketch, "E79.5", {"start": v(-70, -90) * mm, "end": v(70, -90) * mm});
            skArc(sketch, "E79.6", {"start": v(70, -90) * mm, "mid": v(77.07, -87.07) * mm, "end": v(80, -80) * mm});
            skLineSegment(sketch, "E79.7", {"start": v(80, -80) * mm, "end": v(80, 80) * mm});
            skLineSegment(sketch, "E79.8", {"start": v(-70, 90) * mm, "end": v(70, 90) * mm});
            skArc(sketch, "E79.9", {"start": v(-70, 90) * mm, "mid": v(-77.07, 87.07) * mm, "end": v(-80, 80) * mm});
            skLineSegment(sketch, "E79.10", {"start": v(-57, 40.3) * mm, "end": v(-57, -40.3) * mm});
            skLineSegment(sketch, "E79.11", {"start": v(57, 40.3) * mm, "end": v(57, -40.3) * mm});
            skArc(sketch, "E79.12", {"start": v(54.3, 45.81) * mm, "mid": v(0, 64.5) * mm, "end": v(-54.3, 45.81) * mm});
            skArc(sketch, "E79.13", {"start": v(-54.3, -45.81) * mm, "mid": v(0, -64.5) * mm, "end": v(54.3, -45.81) * mm});
            skArc(sketch, "E79.14", {"start": v(-54.3, 45.81) * mm, "mid": v(-56.3, 43.36) * mm, "end": v(-57, 40.3) * mm});
            skArc(sketch, "E79.15", {"start": v(54.3, -45.81) * mm, "mid": v(56.3, -43.36) * mm, "end": v(57, -40.3) * mm});
            skArc(sketch, "E79.16", {"start": v(-57, -40.3) * mm, "mid": v(-56.3, -43.36) * mm, "end": v(-54.3, -45.81) * mm});
            skArc(sketch, "E79.17", {"start": v(57, 40.3) * mm, "mid": v(56.3, 43.36) * mm, "end": v(54.3, 45.81) * mm});
            skArc(sketch, "E79.18", {"start": v(-80, -80) * mm, "mid": v(-77.07, -87.07) * mm, "end": v(-70, -90) * mm});
            skArc(sketch, "E79.19", {"start": v(80, 80) * mm, "mid": v(77.07, 87.07) * mm, "end": v(70, 90) * mm});
            skLineSegment(sketch, "E80", {"start": v(0, 90) * mm, "end": v(0, 120) * mm, "construction": true});
            skArc(sketch, "E81", {"start": v(15, 120) * mm, "mid": v(0, 135) * mm, "end": v(-15, 120) * mm});
            skLineSegment(sketch, "E82", {"start": v(-15, 120) * mm, "end": v(-15, 108) * mm});
            skLineSegment(sketch, "E83", {"start": v(-15, 108) * mm, "end": v(-33, 90) * mm});
            skLineSegment(sketch, "E84.MirrorCS", {"start": v(15, 120) * mm, "end": v(15, 108) * mm});
            skLineSegment(sketch, "E85.MirrorCS", {"start": v(15, 108) * mm, "end": v(33, 90) * mm});
            skLineSegment(sketch, "E86", {"start": v(-80, 0) * mm, "end": v(80, 0) * mm, "construction": true});
            skCircle(sketch, "E87", {"center": v(0, 120) * mm, "radius": 6 * mm});
            skArc(sketch, "E88.MirrorCS", {"start": v(-15, 120) * mm, "mid": v(0, 135) * mm, "end": v(15, 120) * mm});
            skLineSegment(sketch, "E89.MirrorCS", {"start": v(0, -90) * mm, "end": v(0, -120) * mm, "construction": true});
            skLineSegment(sketch, "E90.MirrorCS", {"start": v(-15, -108) * mm, "end": v(-33, -90) * mm});
            skLineSegment(sketch, "E91.MirrorCS", {"start": v(15, -108) * mm, "end": v(33, -90) * mm});
            skLineSegment(sketch, "E92.MirrorCS", {"start": v(15, -120) * mm, "end": v(15, -108) * mm});
            skCircle(sketch, "E93.MirrorC", {"center": v(0, -120) * mm, "radius": 6 * mm});
            skArc(sketch, "E94.MirrorCS", {"start": v(15, -120) * mm, "mid": v(0, -135) * mm, "end": v(-15, -120) * mm});
            skLineSegment(sketch, "E95.MirrorCS", {"start": v(-15, -120) * mm, "end": v(-15, -108) * mm});
            skArc(sketch, "E96.MirrorCS", {"start": v(-15, -120) * mm, "mid": v(0, -135) * mm, "end": v(15, -120) * mm});
            skSolve(sketch);
        }
        {
            var Q0;
            {var subQ1=sQuery(id+"F16.wireOp",EDGE,"E83");Q0=makeQuery(id+"F16.imprint","IMPRINT",FACE,{"disambiguationData":[TD([[makeQuery(id+"F16.imprint","IMPRINT",EDGE,{"derivedFrom":subQ1}),1.0]])]});}
            var Q1;
            Q1=makeQuery(id+"F16.imprint","IMPRINT",FACE,{"disambiguationData":[TD([[makeQuery(id+"F16.imprint","IMPRINT",EDGE,{"derivedFrom":sQuery(id+"F16.wireOp",EDGE,"E79.0")}),-1.0]])]});
            var Q2;
            {var subQ0=sQuery(id+"F16.wireOp",EDGE,"E90.MirrorCS");Q2=makeQuery(id+"F16.imprint","IMPRINT",FACE,{"disambiguationData":[TD([[makeQuery(id+"F16.imprint","IMPRINT",EDGE,{"derivedFrom":subQ0}),-1.0]])]});}
            var Q3;
            Q3=makeQuery(id+"F2.opExtrude","CAP_FACE",FACE,{"disambiguationData":[OSD([sQuery(id+"F0.wireOp",EDGE,"E12"),sQuery(id+"F0.wireOp",EDGE,"E13"),sQuery(id+"F0.wireOp",EDGE,"E14"),sQuery(id+"F0.wireOp",EDGE,"E15"),sQuery(id+"F0.wireOp",EDGE,"E17.filletArc"),sQuery(id+"F0.wireOp",EDGE,"E18.filletArc"),sQuery(id+"F0.wireOp",EDGE,"E19.filletArc"),sQuery(id+"F0.wireOp",EDGE,"E20.filletArc"),sQuery(id+"F0.wireOp",EDGE,"E25.0"),sQuery(id+"F0.wireOp",EDGE,"E25.1"),sQuery(id+"F0.wireOp",EDGE,"E25.2"),sQuery(id+"F0.wireOp",EDGE,"E25.3"),sQuery(id+"F0.wireOp",EDGE,"E25.4"),sQuery(id+"F0.wireOp",EDGE,"E25.5"),sQuery(id+"F0.wireOp",EDGE,"E25.6"),sQuery(id+"F0.wireOp",EDGE,"E25.7")])],"isStart":false});
            extrude(context, id + "F17", {"entities" : qUnion([Q0, Q1, Q2]), "endBound" : BoundingType.UP_TO_SURFACE, "depth" : 25 * mm, "endBoundEntityFace" : qUnion([Q3]), "offsetDistance" : 25 * mm});
        }
    });
